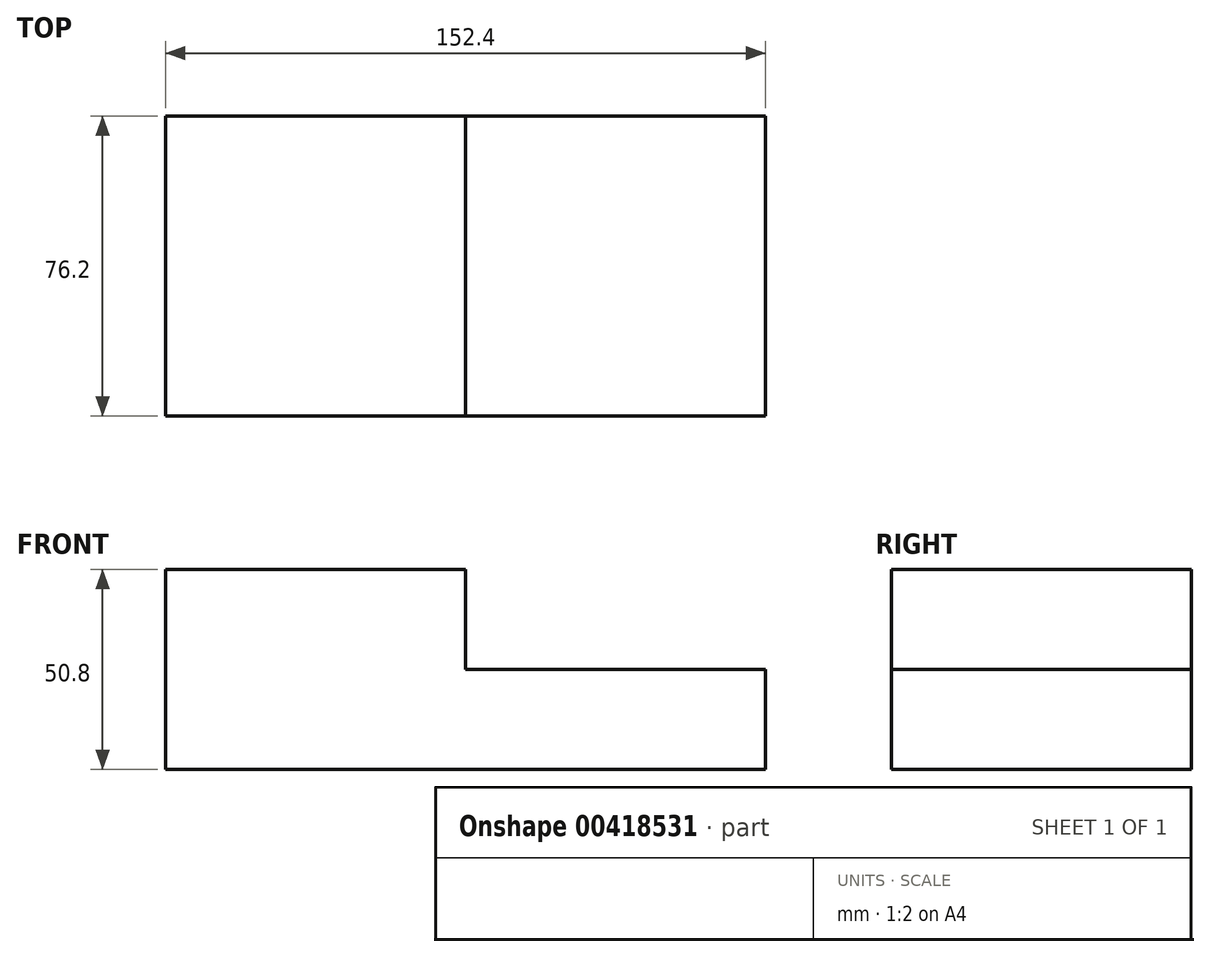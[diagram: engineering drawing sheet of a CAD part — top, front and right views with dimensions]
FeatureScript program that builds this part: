
annotation { "Feature Type Name" : "Feature", "Feature Type Description" : "" }
export const myFeature = defineFeature(function(context is Context, id is Id, definition is map)
    precondition{}
    {
        {
            var Q0;
            Q0=qCreatedBy(makeId("Front.planeOp"),FACE);
            var sketch = newSketch(context, id + "F0", { "sketchPlane" : qUnion([Q0])});
            skLineSegment(sketch, "E0", {"start": v(0, 0) * mm, "end": v(152.4, 0) * mm});
            skLineSegment(sketch, "E1", {"start": v(0, 0) * mm, "end": v(0, 50.8) * mm});
            skLineSegment(sketch, "E2", {"start": v(0, 50.8) * mm, "end": v(76.2, 50.8) * mm});
            skLineSegment(sketch, "E3", {"start": v(76.2, 50.8) * mm, "end": v(76.2, 25.4) * mm});
            skLineSegment(sketch, "E4", {"start": v(76.2, 25.4) * mm, "end": v(152.4, 25.4) * mm});
            skLineSegment(sketch, "E5", {"start": v(152.4, 25.4) * mm, "end": v(152.4, 0) * mm});
            skSolve(sketch);
        }
        {
            var Q0;
            Q0=makeQuery(id+"F0.imprint","IMPRINT",FACE,{"disambiguationData":[TD([[makeQuery(id+"F0.imprint","IMPRINT",EDGE,{"derivedFrom":sQuery(id+"F0.wireOp",EDGE,"E0")}),1.0]])]});
            extrude(context, id + "F1", {"entities" : qUnion([Q0]), "depth" : 76.2 * mm});
        }
    });
